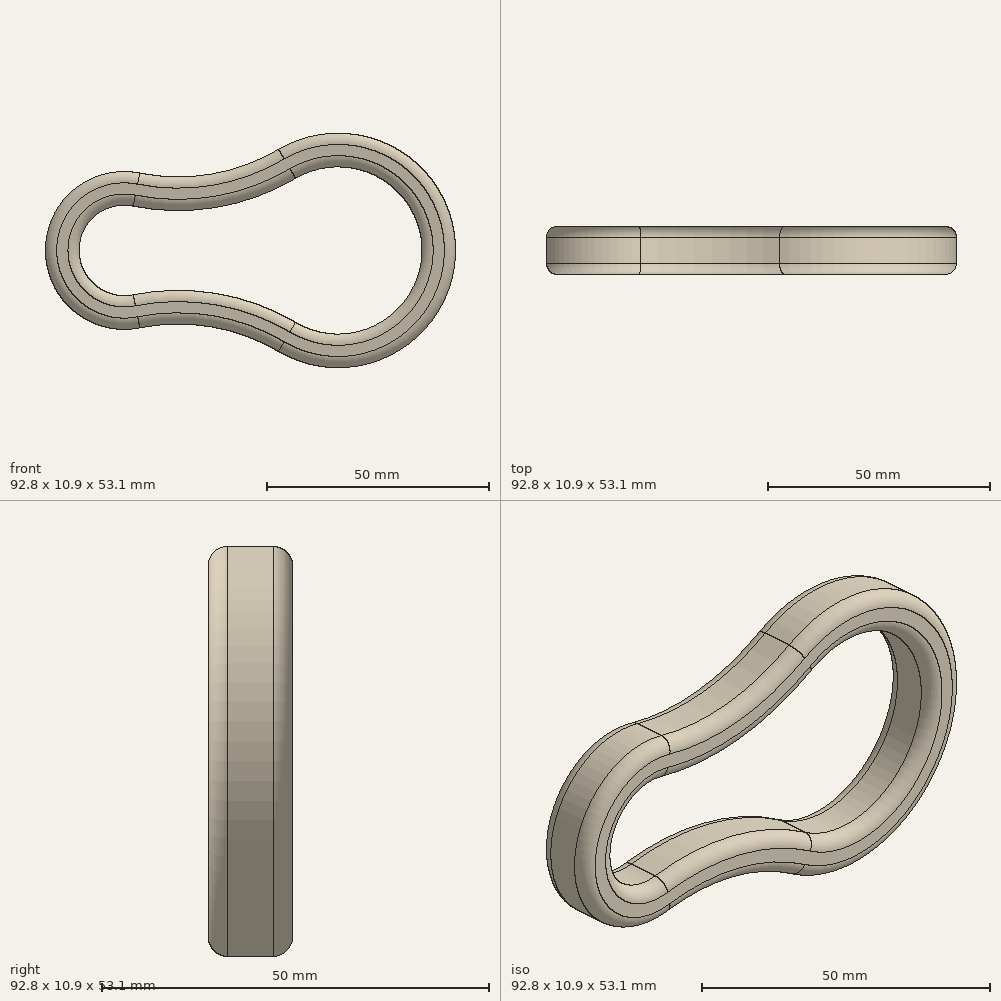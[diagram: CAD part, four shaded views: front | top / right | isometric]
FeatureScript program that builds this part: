
annotation { "Feature Type Name" : "Feature", "Feature Type Description" : "" }
export const myFeature = defineFeature(function(context is Context, id is Id, definition is map)
    precondition{}
    {
        {
            var Q0;
            Q0=qCreatedBy(makeId("Front.planeOp"),FACE);
            var sketch = newSketch(context, id + "F0", { "sketchPlane" : qUnion([Q0])});
            skArc(sketch, "E0", {"start": v(2, 10.03) * mm, "mid": v(-10.23, 0) * mm, "end": v(2, -10.03) * mm});
            skArc(sketch, "E1", {"start": v(38.76, -16.28) * mm, "mid": v(67.3, 0) * mm, "end": v(38.76, 16.28) * mm});
            skArc(sketch, "E2", {"start": v(2, 10.03) * mm, "mid": v(20.96, 9.75) * mm, "end": v(38.76, 16.28) * mm});
            skArc(sketch, "E3", {"start": v(38.76, -16.28) * mm, "mid": v(20.96, -9.75) * mm, "end": v(2, -10.03) * mm});
            skArc(sketch, "E4.0", {"start": v(34.88, -22.83) * mm, "mid": v(74.92, 0) * mm, "end": v(34.88, 22.83) * mm});
            skArc(sketch, "E4.1", {"start": v(34.88, -22.83) * mm, "mid": v(19.69, -17.27) * mm, "end": v(3.5, -17.5) * mm});
            skArc(sketch, "E4.2", {"start": v(3.5, 17.5) * mm, "mid": v(-17.85, 0) * mm, "end": v(3.5, -17.5) * mm});
            skArc(sketch, "E4.3", {"start": v(3.5, 17.5) * mm, "mid": v(19.69, 17.27) * mm, "end": v(34.88, 22.83) * mm});
            skSolve(sketch);
        }
        {
            var Q0;
            Q0 = qSketchRegion(id + "F0", true);
            extrude(context, id + "F1", {"entities" : qUnion([Q0]), "depth" : 10.92 * mm});
        }
        {
            var Q0;
            Q0=makeQuery(id+"F1.opExtrude","CAP_EDGE",EDGE,{"disambiguationData":[OSD([sQuery(id+"F0.wireOp",EDGE,"E4.0")])],"isStart":false});
            var Q1;
            Q1=makeQuery(id+"F1.opExtrude","CAP_EDGE",EDGE,{"disambiguationData":[OSD([sQuery(id+"F0.wireOp",EDGE,"E4.3")])],"isStart":true});
            var Q2;
            Q2=makeQuery(id+"F1.opExtrude","CAP_EDGE",EDGE,{"disambiguationData":[OSD([sQuery(id+"F0.wireOp",EDGE,"E1")])],"isStart":false});
            var Q3;
            Q3=makeQuery(id+"F1.opExtrude","CAP_EDGE",EDGE,{"disambiguationData":[OSD([sQuery(id+"F0.wireOp",EDGE,"E3")])],"isStart":true});
            fillet(context, id + "F2", {"entities" : qUnion([Q0, Q1, Q2, Q3]), "radius" : 2.54 * mm, "tangentPropagation" : true, "allowEdgeOverflow" : false});
        }
    });
